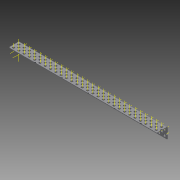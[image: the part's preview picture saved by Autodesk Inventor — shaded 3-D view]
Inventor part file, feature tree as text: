
AUTODESK INVENTOR PART (.ipt)
format: ipt  version: 2015 (Build 190159000, 159)  size: 2,258,944 bytes
history: native  units: in
note: dims shown in document units (in); Inventor stores cm internally (conversion verified against a paired STEP export)
features: other x173, pattern_linear x4, sheet_metal_op x1, extrude x1, imported_body x1, sketch x1
ambient origin geometry x8: Origin, YZ Plane, XZ Plane, XY Plane, X Axis, Y Axis, Z Axis, Center Point
bodies: Body1 (feature_tree)
feature tree (181):
  sheet_metal_op  "Fold1"
  other  "L-Channel"
  extrude  "length cut"  Depth=0.5in
  other  "top out axis"
  other  "top inner axis"
  other  "back out axis"
  other  "back inner axis"
  pattern_linear  "top outer axes"  Count1=2 Spacing1=0.5in
  pattern_linear  "top inner axes"  Spacing1=0.5in  [1 undecoded]
  pattern_linear  "back outer axes"  Count1=2 Spacing1=0.5in
  pattern_linear  "back inner axes"  Spacing1=0.5in  [1 undecoded]
  other  "right plane"
  imported_body  "Base1"
  sketch  "Sketch1"  dims[d1=0.0in d4=0.5in d5=0.7874in d7=0.5in d10=0.5in d13=0.5in d14=0.7874in d16=0.5in d19=0.5in d20=-14.0in d21=0.0in d22=0.0in d23=0.0in d24=0.0in d25=0.0in d26=0.0in]
  other  "Work Point1"
  other  "Work Point2"
  other  "Work Point3"
  other  "Work Point4"
  other  "Work Axis5"
  other  "Work Axis6"
  other  "Work Axis7"
  other  "Work Axis8"
  other  "Work Axis11"
  other  "Work Axis12"
  other  "Work Axis13"
  other  "Work Axis14"
  other  "Work Axis15"
  other  "Work Axis18"
  other  "Work Axis19"
  other  "Work Axis20"
  other  "Work Axis23"
  other  "Work Axis24"
  other  "Work Axis25"
  other  "Work Axis26"
  other  "Work Axis29"
  other  "Work Axis30"
  other  "Work Axis31"
  other  "Work Axis32"
  other  "Work Axis33"
  other  "Work Axis36"
  other  "Work Axis37"
  other  "Work Axis38"
  other  "Work Axis41"
  other  "Work Axis42"
  other  "Work Axis43"
  other  "Work Axis44"
  other  "Work Axis45"
  other  "Work Axis46"
  other  "Work Axis47"
  other  "Work Axis48"
  other  "Work Axis49"
  other  "Work Axis50"
  other  "Work Axis51"
  other  "Work Axis52"
  other  "Work Axis53"
  other  "Work Axis54"
  other  "Work Axis55"
  other  "Work Axis56"
  other  "Work Axis57"
  other  "Work Axis58"
  other  "Work Axis59"
  other  "Work Axis60"
  other  "Work Axis61"
  other  "Work Axis62"
  other  "Work Axis63"
  other  "Work Axis64"
  other  "Work Axis65"
  other  "Work Axis66"
  other  "Work Axis67"
  other  "Work Axis68"
  other  "Work Axis69"
  other  "Work Axis70"
  other  "Work Axis71"
  other  "Work Axis72"
  other  "Work Axis73"
  other  "Work Axis74"
  other  "Work Axis75"
  other  "Work Axis76"
  other  "Work Axis77"
  other  "Work Axis78"
  other  "Work Axis79"
  other  "Work Axis80"
  other  "Work Axis81"
  other  "Work Axis82"
  other  "Work Axis83"
  other  "Work Axis84"
  other  "Work Axis85"
  other  "Work Axis86"
  other  "Work Axis87"
  other  "Work Axis88"
  other  "Work Axis89"
  other  "Work Axis90"
  other  "Work Axis91"
  other  "Work Axis92"
  other  "Work Axis93"
  other  "Work Axis94"
  other  "Work Axis95"
  other  "Work Axis96"
  other  "Work Axis97"
  other  "Work Axis98"
  other  "Work Axis99"
  other  "Work Axis100"
  other  "Work Axis101"
  other  "Work Axis102"
  other  "Work Axis103"
  other  "Work Axis104"
  other  "Work Axis105"
  other  "Work Axis106"
  other  "Work Axis107"
  other  "Work Axis108"
  other  "Work Axis109"
  other  "Work Axis110"
  other  "Work Axis111"
  other  "Work Axis112"
  other  "Work Axis113"
  other  "Work Axis114"
  other  "Work Axis115"
  other  "Work Axis116"
  other  "Work Axis117"
  other  "Work Axis118"
  other  "Work Axis119"
  other  "Work Axis120"
  other  "Work Axis121"
  other  "Work Axis122"
  other  "Work Axis123"
  other  "Work Axis124"
  other  "Work Axis125"
  other  "Work Axis126"
  other  "Work Axis127"
  other  "Work Axis128"
  other  "Work Axis129"
  other  "Work Axis130"
  other  "Work Axis131"
  other  "Work Axis132"
  other  "Work Axis133"
  other  "Work Axis134"
  other  "Work Axis135"
  other  "Work Axis136"
  other  "Work Axis137"
  other  "Work Axis138"
  other  "Work Axis139"
  other  "Work Axis140"
  other  "Work Axis141"
  other  "Work Axis142"
  other  "Work Axis143"
  other  "Work Axis144"
  other  "Work Axis145"
  other  "Work Axis146"
  other  "Work Axis147"
  other  "Work Axis148"
  other  "Work Axis149"
  other  "Work Axis150"
  other  "Work Axis151"
  other  "Work Axis152"
  other  "Work Axis153"
  other  "Work Axis154"
  other  "Work Axis155"
  other  "Work Axis156"
  other  "Work Axis157"
  other  "Work Axis158"
  other  "Work Axis159"
  other  "Work Axis160"
  other  "left plane"
  other  "Work Axis161"
  other  "Work Axis162"
  other  "Work Axis163"
  other  "Work Axis164"
  other  "Work Axis165"
  other  "Work Axis166"
  other  "Work Axis167"
  other  "Work Axis168"
  other  "Work Axis169"
  other  "Work Axis170"
  other  "Work Axis171"
  other  "Work Axis172"
  other  "Work Axis173"
  other  "Work Axis174"
  other  "Work Axis175"
  other  "Work Axis176"
  other  "Work Axis177"
  other  "Work Axis178"
note: 2 required parameter values undecoded (feature->parameter linkage not recoverable at this tier; creation-order binding heuristic only, values carry confidence <= 0.55)
